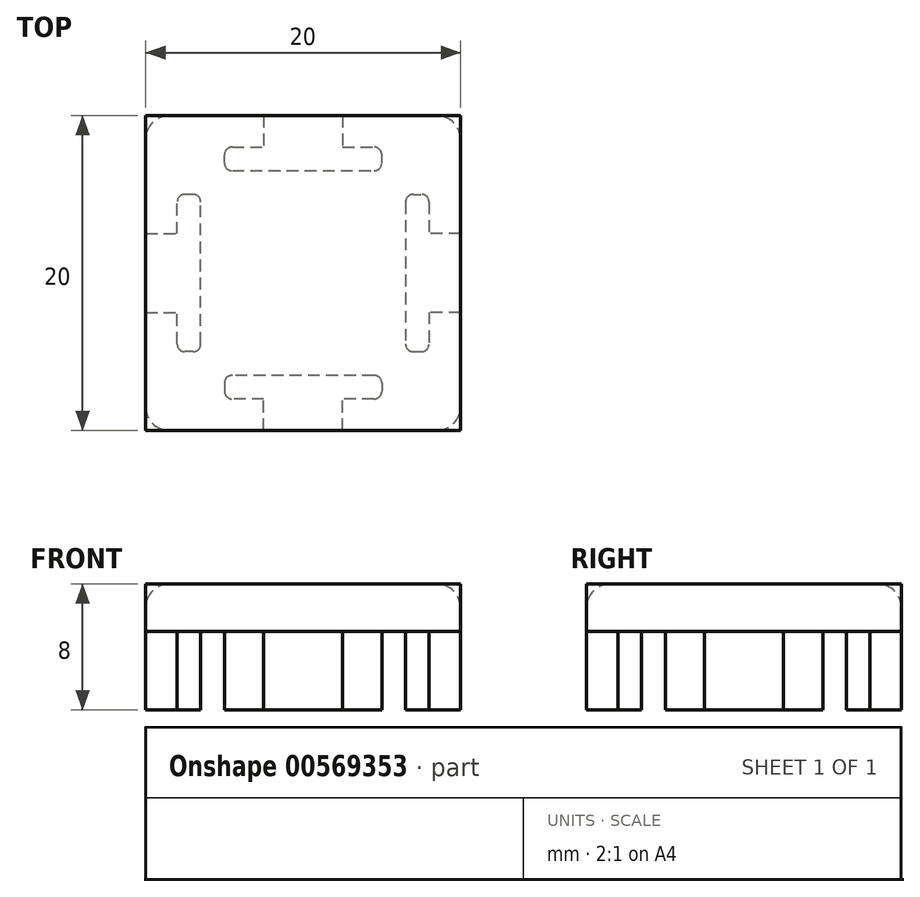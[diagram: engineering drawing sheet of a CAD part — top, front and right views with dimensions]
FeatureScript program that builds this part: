
annotation { "Feature Type Name" : "Feature", "Feature Type Description" : "" }
export const myFeature = defineFeature(function(context is Context, id is Id, definition is map)
    precondition{}
    {
        {
            var Q0;
            Q0=qCreatedBy(makeId("Top.planeOp"),FACE);
            var sketch = newSketch(context, id + "F0", { "sketchPlane" : qUnion([Q0])});
            skLineSegment(sketch, "E0.bottom", {"start": v(10, 10) * mm, "end": v(-10, 10) * mm});
            skLineSegment(sketch, "E0.top", {"start": v(10, -10) * mm, "end": v(-10, -10) * mm});
            skLineSegment(sketch, "E0.left", {"start": v(10, 10) * mm, "end": v(10, -10) * mm});
            skLineSegment(sketch, "E0.right", {"start": v(-10, 10) * mm, "end": v(-10, -10) * mm});
            skPoint(sketch, "E0.middle", {"position": v(0, 0) * mm});
            skSolve(sketch);
        }
        {
            var Q0;
            Q0 = qSketchRegion(id + "F0", true);
            extrude(context, id + "F1", {"entities" : qUnion([Q0]), "depth" : 3 * mm, "offsetDistance" : 25 * mm});
        }
        {
            var Q0;
            Q0=makeQuery(id+"F1.opExtrude","CAP_FACE",FACE,{"disambiguationData":[OSD([sQuery(id+"F0.wireOp",EDGE,"E0.bottom"),sQuery(id+"F0.wireOp",EDGE,"E0.top"),sQuery(id+"F0.wireOp",EDGE,"E0.left"),sQuery(id+"F0.wireOp",EDGE,"E0.right")])],"isStart":true});
            var sketch = newSketch(context, id + "F2", { "sketchPlane" : qUnion([Q0])});
            skLineSegment(sketch, "E1.left", {"start": v(-2.5, -10) * mm, "end": v(-2.5, -8) * mm});
            skLineSegment(sketch, "E1.right", {"start": v(2.5, -10) * mm, "end": v(2.5, -8) * mm});
            skLineSegment(sketch, "E2.bottom", {"start": v(-4.5, -6.5) * mm, "end": v(4.5, -6.5) * mm});
            skLineSegment(sketch, "E2.top", {"start": v(-4.5, -8) * mm, "end": v(-2.5, -8) * mm});
            skLineSegment(sketch, "E2.left", {"start": v(-5, -7) * mm, "end": v(-5, -7.5) * mm});
            skLineSegment(sketch, "E2.right", {"start": v(5, -7) * mm, "end": v(5, -7.5) * mm});
            skLineSegment(sketch, "E3.trimOffspring", {"start": v(2.5, -8) * mm, "end": v(4.5, -8) * mm});
            skPoint(sketch, "E4.visualSharp", {"position": v(-5, -6.5) * mm});
            skArc(sketch, "E4.filletArc", {"start": v(-4.5, -6.5) * mm, "mid": v(-4.85, -6.65) * mm, "end": v(-5, -7) * mm});
            skPoint(sketch, "E5.visualSharp", {"position": v(-5, -8) * mm});
            skArc(sketch, "E5.filletArc", {"start": v(-5, -7.5) * mm, "mid": v(-4.85, -7.85) * mm, "end": v(-4.5, -8) * mm});
            skPoint(sketch, "E6.visualSharp", {"position": v(5, -6.5) * mm});
            skArc(sketch, "E6.filletArc", {"start": v(5, -7) * mm, "mid": v(4.85, -6.65) * mm, "end": v(4.5, -6.5) * mm});
            skPoint(sketch, "E7.visualSharp", {"position": v(5, -8) * mm});
            skArc(sketch, "E7.filletArc", {"start": v(4.5, -8) * mm, "mid": v(4.85, -7.85) * mm, "end": v(5, -7.5) * mm});
            skLineSegment(sketch, "E8", {"start": v(-2.5, -10) * mm, "end": v(2.5, -10) * mm});
            skSolve(sketch);
        }
        {
            var Q0;
            Q0 = qSketchRegion(id + "F2", true);
            extrude(context, id + "F3", {"entities" : qUnion([Q0]), "operationType" : NewBodyOperationType.ADD, "depth" : 5 * mm, "offsetDistance" : 25 * mm});
        }
        {
            var Q0;
            Q0=qCreatedBy(makeId("Front.planeOp"),FACE);
            var sketch = newSketch(context, id + "F4", { "sketchPlane" : qUnion([Q0])});
            skLineSegment(sketch, "E9", {"start": v(0, 15.47) * mm, "end": v(0, -33.19) * mm, "construction": true});
            skSolve(sketch);
        }
        {
            var Q0;
            Q0=makeQuery(id+"F1.opExtrude","SWEPT_BODY",BODY,{"disambiguationData":[OSD([sQuery(id+"F0.wireOp",EDGE,"E0.bottom"),sQuery(id+"F0.wireOp",EDGE,"E0.top"),sQuery(id+"F0.wireOp",EDGE,"E0.left"),sQuery(id+"F0.wireOp",EDGE,"E0.right")])]});
            var Q1;
            Q1=sQuery(id+"F4.wireOp",EDGE,"E9");
            circularPattern(context, id + "F5", {"entities" : qUnion([Q0]), "axis" : qUnion([Q1]), "angle" : 360 * degree, "instanceCount" : 4, "equalSpace" : true});
        }
        {
            var Q0;
            Q0=makeQuery(id+"F1.opExtrude","CAP_EDGE",EDGE,{"disambiguationData":[OSD([sQuery(id+"F0.wireOp",EDGE,"E0.right")])],"isStart":false});
            var Q1;
            Q1=makeQuery(id+"F1.opExtrude","CAP_EDGE",EDGE,{"disambiguationData":[OSD([sQuery(id+"F0.wireOp",EDGE,"E0.bottom")])],"isStart":false});
            var Q2;
            Q2=makeQuery(id+"F1.opExtrude","CAP_EDGE",EDGE,{"disambiguationData":[OSD([sQuery(id+"F0.wireOp",EDGE,"E0.top")])],"isStart":false});
            var Q3;
            Q3=makeQuery(id+"F1.opExtrude","CAP_EDGE",EDGE,{"disambiguationData":[OSD([sQuery(id+"F0.wireOp",EDGE,"E0.left")])],"isStart":false});
            var Q4;
            Q4=makeQuery(id+"F1.opExtrude","SWEPT_EDGE",EDGE,{"disambiguationData":[OSD([sQuery(id+"F0.wireOp",EDGE,"E0.top"),sQuery(id+"F0.wireOp",EDGE,"E0.left")])]});
            var Q5;
            Q5=makeQuery(id+"F1.opExtrude","SWEPT_EDGE",EDGE,{"disambiguationData":[OSD([sQuery(id+"F0.wireOp",EDGE,"E0.bottom"),sQuery(id+"F0.wireOp",EDGE,"E0.left")])]});
            var Q6;
            Q6=makeQuery(id+"F1.opExtrude","SWEPT_EDGE",EDGE,{"disambiguationData":[OSD([sQuery(id+"F0.wireOp",EDGE,"E0.bottom"),sQuery(id+"F0.wireOp",EDGE,"E0.right")])]});
            var Q7;
            Q7=makeQuery(id+"F1.opExtrude","SWEPT_EDGE",EDGE,{"disambiguationData":[OSD([sQuery(id+"F0.wireOp",EDGE,"E0.top"),sQuery(id+"F0.wireOp",EDGE,"E0.right")])]});
            fillet(context, id + "F6", {"entities" : qUnion([Q0, Q1, Q2, Q3, Q4, Q5, Q6, Q7]), "radius" : 1.5 * mm, "tangentPropagation" : true, "allowEdgeOverflow" : false});
        }
    });
